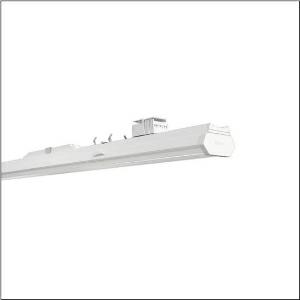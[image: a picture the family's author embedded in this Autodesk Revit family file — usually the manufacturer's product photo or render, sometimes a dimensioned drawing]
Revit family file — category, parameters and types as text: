
# Revit family: licross_11_protected_mo_51tp11dn695g
name_source: partatom
category: Lighting Fixtures
units: mm (PartAtom-declared; Revit-internal decimal feet)

## family parameters
Cut with Voids When Loaded = No
Host = Face
Light Source = No
Part Type = Normal
Room Calculation Point = No
Round Connector Dimension = Use Diameter
Shared = No

## types (1)
- --- (1 x LED, 9680 lm, 57.1 W, 6500K)
    Apparent Load = 57 VA
    CIE Flux Codes = 83 94 98 100 100
    Color Rendering = 80
    Color Temperature = 6500K
    Default Elevation = 1800 mm
    Description = Licross 11 Protected MO, luminaire insert, of sheet steel, galvanised, coil coated, white, length: 1.500mm, width: 90mm, height: 101mm, LED rated luminous flux: 9.680lm, light colour: 865, SDCM (Standard Deviation of Colour Matching)MacAdam ≤ 2 SDCM (initial), control gear: DALI 2, with plug, 5-pole, with phase selection, mains connection: 220..240V, AC, 50/60Hz, rated input power: 57W, internal wiring halogen-free, primary light control with lens, of plastic, primary optical cover: cover, of PMMA, light emission: direct distribution, primary light characteristic: symmetric, protection rating (complete): IP64, insulation class (complete): insulation class I (protective earthing), certification: CE, ENEC, VDE, UKCA, protection symbol: D if used in an environment with conductive dust loads with corresponding accessories, impact resistance: IK06, permissible ambient temperature for indoor applications: -25..+35°C, corresponds to IFS (International Featured Standards) requirements for safety and quality in the food industry, reducing of maximum allowable ambient temperature of 5°C with ceiling mounting, LABS conformity tested according to VDMA 24364:2018-05, The light source and the operating device comply with the requirements of the Ecodesign Regulation (EU) 2019/2020 and are replaceable in accordance with this regulation, packaging unit: 1 piece
    Height = 92 mm
    Lamp = 1 x LED
    Lamp Light Flux = 9680 lm
    Lamp Power = 57.1 W
    Lamp count = 1
    Length = 1500 mm
    Luminous efficacy = 170 lm/W
    Manufacturer = Siteco
    ModVariant = No
    Model = 51TP11DN695G
    Mounting Place = Ceiling
    Mounting Type = Pendant
    Number of Poles = 1
    OnlyDefault = Yes
    Power Factor = 1
    Product Name = Licross 11 Protected MO
    Product group = luminaire insert | ceiling pendant
    ProductGroupID = 901
    Protection Class = Protection class I
    Protection Degree = IP 64
    RLX_Detail_Level = 1
    RLX_Emergency_Light_Flux = 0 lm
    RLX_Emergency_Type = 0
    RLX_Emergency_Type_DB = No
    RlxData = <blob elided: 24397 chars, md5=485d8ec7>
    Socket = socket
    Standby Power = 0 W
    System Light Flux = 9680 lm
    System Power = 57 W
    Type Comments = factory setting: luminous flux: 100 % | dim-lin: 254 | 378 mA
    Type Image = l_1256148.jpg
    URL = http://relux.com
    VarID = @adj_056115
    Voltage = 0 V
    Weight = 0.00 kg
    Width = 88 mm

## geometry (parser evidence)
native form markers: Blend x4, Sweep x12
no freeform markers — native parametric forms only
